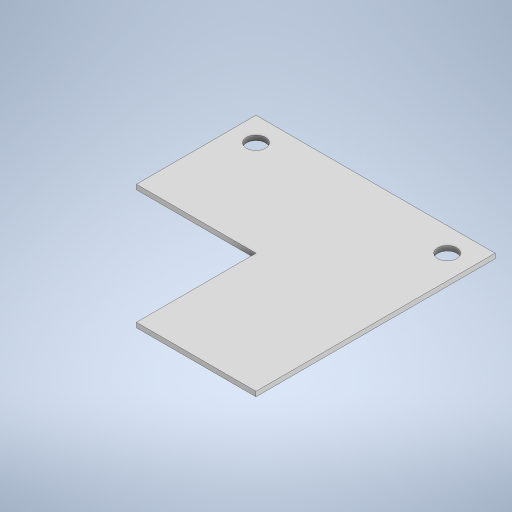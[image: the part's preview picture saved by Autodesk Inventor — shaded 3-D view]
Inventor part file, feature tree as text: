
AUTODESK INVENTOR PART (.ipt)
format: ipt  version: 2023 (Build 270158000, 158)  size: 231,936 bytes
history: native  units: mm
features: extrude x1
ambient origin geometry x8: Origin, YZ Plane, XZ Plane, XY Plane, X Axis, Y Axis, Z Axis, Center Point
bodies: Solid1 (feature_tree)
feature tree (1):
  extrude  "Extrusion1"  Depth=100.0mm
